# Revit family: Hager-Vega-IP30-syst-NL-en
name_source: partatom
category: Electrical Equipment
units: mm (PartAtom-declared; Revit-internal decimal feet)

## family parameters
Cut with Voids When Loaded = No
Host = Face
Panel Configuration = Two Columns, Circuits Across
Part Type = Panelboard
Room Calculation Point = No
Round Connector Dimension = Use Diameter
Shared = No

## types (8) — shared parameters
EF000003 - Mounting method = EV000384 - Surface mounted (plaster)
EF000007 - Colour = EV000202 - White
EF000008 - Width = 400 mm  [stored 1.31234 ft]
EF000049 - Depth = 146 mm  [stored 0.479003 ft]
EF000116 - RAL-number = 9010
EF000118 - With mounting plate = No
EF000339 - Type of cover = EV004216 - Door
EF001062 - EMC-version = No
EF001088 - Extension possible = Yes
EF001131 - Internal depth = 120 mm
EF001134 - DIN-rail = Yes
EF001596 - Material housing = EV000139 - Plastic
EF002950 - Width in number of modular spacings = 18
EF004462 - Type of closure = EV000154 - Other
EF005474 - Degree of protection (IP) = EV006410 - IP30
EF006306 - With lock = No
EF009212 - Cover model = EV000116 - Closed
EF015776 - Earthing terminal block = Yes
EF015777 - Neutral terminal block = No
EF015941 - Signal passing door = Yes
HG000001 - Number of columns = 1
HG000002 - With door or cover = Yes
HG000003 - Range = Vega
HG000005 - Thickness = 3 mm  [stored 0.00984252 ft]
HG000006 - Flush mounted = No
HG000009 - Double swing door = No
HG000010 - Asymmetric doors = No
HG000011 - Empty rows from bottom = No
HG000017 - Distance between poles = 18 mm  [stored 0.0590551 ft]
Manufacturer = Hager
Type Comments = Vega
zero-valued in all types: Default Elevation, EF000218 - Built-in depth, EF000332 - Built-in height, EF000846 - Built-in width, HG000007 - Number of empty columns, HG000008 - Number of empty rows

## per-type parameters (varying)
| type | EF000040 - Height | EF000266 - Number of rows | EF006244 - Transparent cover/door | HG000004 - Manufacturer reference | Model |
| Surface mounted IP30 W400 H325 D146 18 Modular spacings - VB118C | 325 mm | 1 | No | VB118C | VB118C |
| Surface mounted IP30 W400 H325 D146 18 Modular spacings - VB118P | 325 mm | 1 | Yes | VB118P | VB118P |
| Surface mounted IP30 W400 H475 D146 18 Modular spacings - VB218C | 475 mm  [stored 1.5584 ft] | 2 | No | VB218C | VB218C |
| Surface mounted IP30 W400 H475 D146 18 Modular spacings - VB218P | 475 mm  [stored 1.5584 ft] | 2 | Yes | VB218P | VB218P |
| Surface mounted IP30 W400 H625 D146 18 Modular spacings - VB318C | 625 mm  [stored 2.05052 ft] | 3 | No | VB318C | VB318C |
| Surface mounted IP30 W400 H625 D146 18 Modular spacings - VB318P | 625 mm  [stored 2.05052 ft] | 3 | Yes | VB318P | VB318P |
| Surface mounted IP30 W400 H775 D146 18 Modular spacings - VB418C | 775 mm  [stored 2.54265 ft] | 4 | No | VB418C | VB418C |
| Surface mounted IP30 W400 H775 D146 18 Modular spacings - VB418P | 775 mm  [stored 2.54265 ft] | 4 | Yes | VB418P | VB418P |

note: [stored X ft] marks values corroborated as IEEE doubles in the binary element streams (Revit-internal decimal feet)

## geometry (parser evidence)
native form markers: Sweep x17
no freeform markers — native parametric forms only
